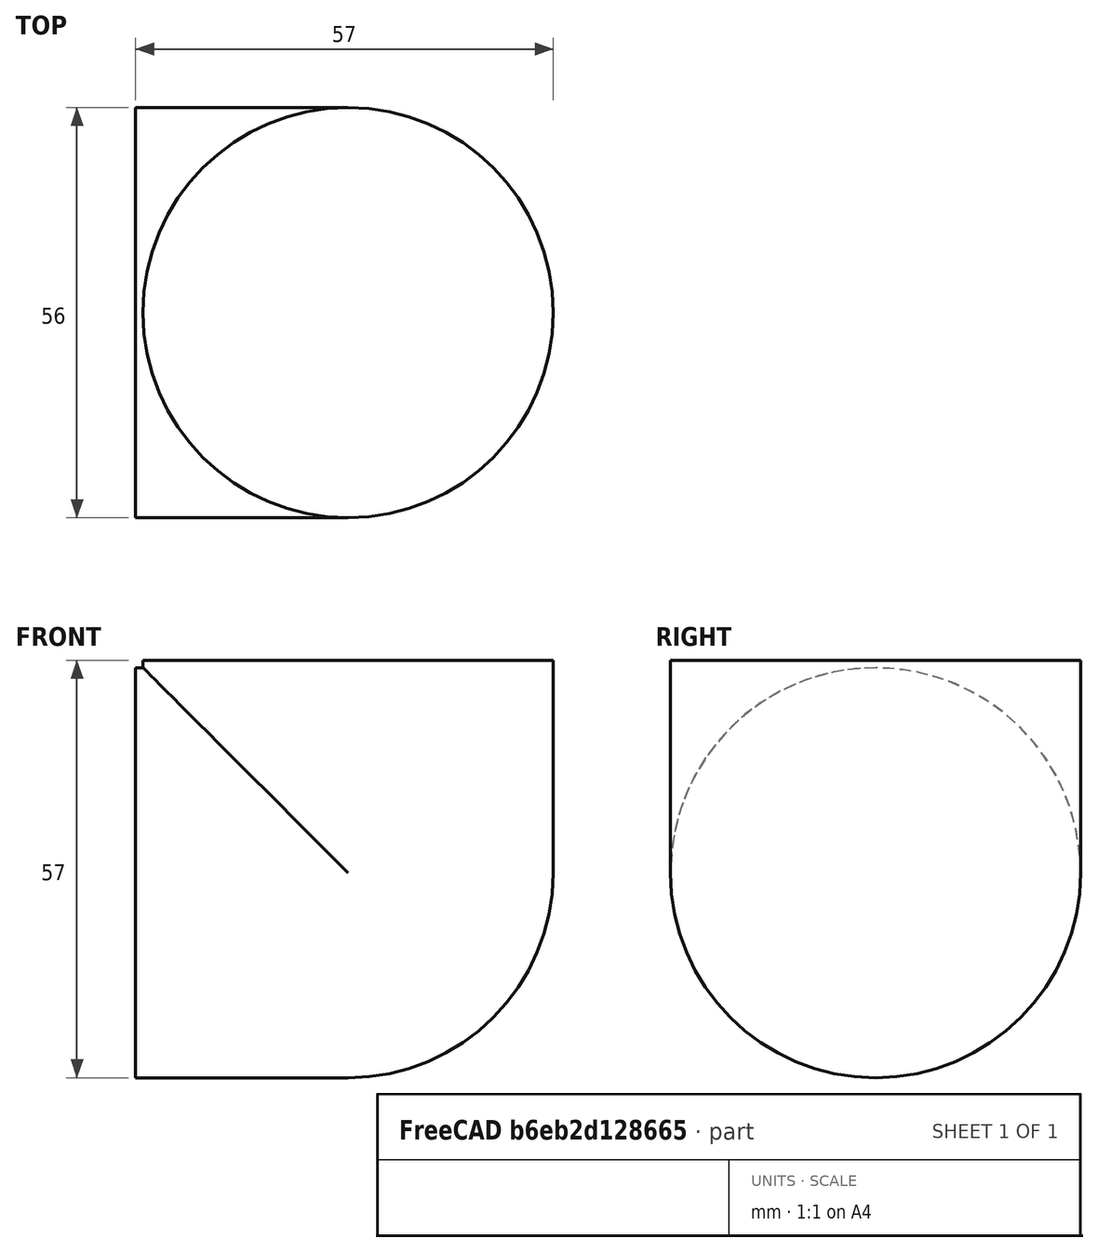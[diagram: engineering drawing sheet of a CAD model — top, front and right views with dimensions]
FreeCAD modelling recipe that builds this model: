
FCSTD DOCUMENT  (FreeCAD 0.21R33668 +26 (Git))
Label: arm-subpart-angle
License: All rights reserved
LicenseURL: http://en.wikipedia.org/wiki/All_rights_reserved
objects: Part::Cylinder×2, Part::Sphere×1, Part::MultiFuse×1, App::Part×1
note: 4 computed .brp shape members not serialized (recipe doc carries the construction recipe); baked Part::Feature solids carry a one-line shape summary decoded from their .brp

FEATURE [Part::Sphere] Sphere
  Angle1 = -90
  Angle2 = 90
  Angle3 = 360
  AttacherType = Attacher::AttachEngine3D
  Placement = pos=(28,0,0) rot=(0,0,1;0rad)
  Radius = 28
FEATURE [Part::Cylinder] Cylinder
  Angle = 360
  AttacherType = Attacher::AttachEngine3D
  FirstAngle = 0
  Height = 29
  Placement = pos=(28,0,0) rot=(0,0,1;0rad)
  Radius = 28
  SecondAngle = 0
FEATURE [Part::Cylinder] Cylinder001
  Angle = 360
  AttacherType = Attacher::AttachEngine3D
  FirstAngle = 0
  Height = 29
  Placement = pos=(28,0,0) rot=(0,-1,0;1.5708rad)
  Radius = 28
  SecondAngle = 0
FEATURE [Part::MultiFuse] Fusion
  Shapes = -> [Cylinder001,Cylinder,Sphere]
FEATURE [App::Part] Part  label="angle"
  Group = -> [Cylinder001,Cylinder,Sphere,Fusion]
  Origin = -> Origin
